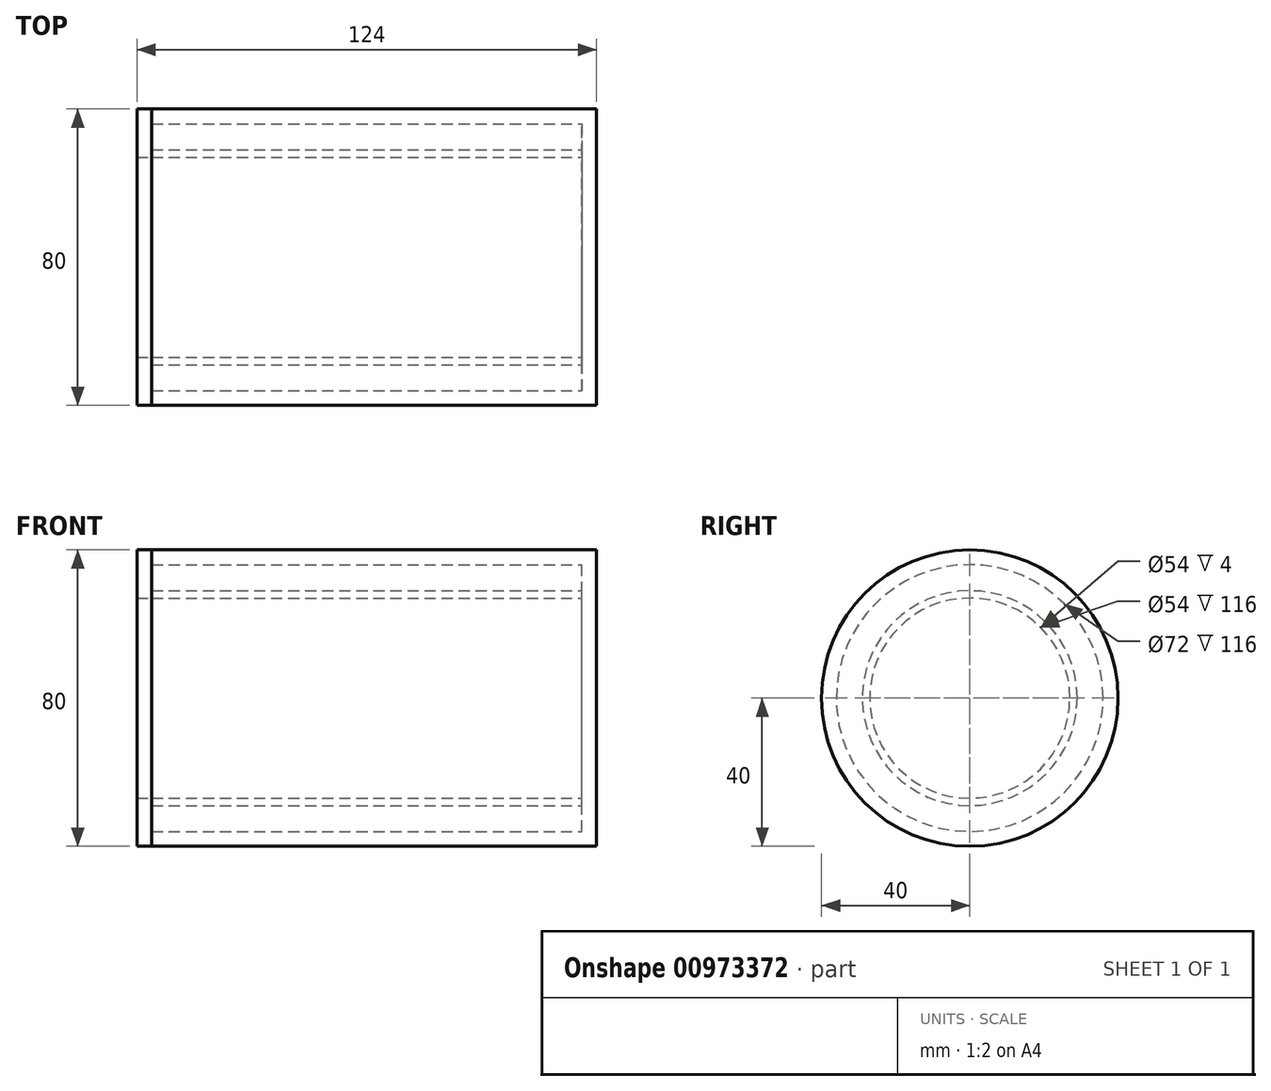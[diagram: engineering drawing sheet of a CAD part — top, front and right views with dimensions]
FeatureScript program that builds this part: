
annotation { "Feature Type Name" : "Feature", "Feature Type Description" : "" }
export const myFeature = defineFeature(function(context is Context, id is Id, definition is map)
    precondition{}
    {
        {
            var Q0;
            Q0=qCreatedBy(makeId("Front.planeOp"),FACE);
            var sketch = newSketch(context, id + "F0", { "sketchPlane" : qUnion([Q0])});
            skLineSegment(sketch, "E0.bottom", {"start": v(60, -2) * mm, "end": v(-60, -2) * mm});
            skLineSegment(sketch, "E0.top", {"start": v(60, 2) * mm, "end": v(-60, 2) * mm});
            skLineSegment(sketch, "E0.left", {"start": v(60, -2) * mm, "end": v(60, 2) * mm});
            skPoint(sketch, "E0.middle", {"position": v(0, 0) * mm});
            skLineSegment(sketch, "E1.bottom", {"start": v(60, -2) * mm, "end": v(56, -2) * mm});
            skLineSegment(sketch, "E1.top", {"start": v(60, -38) * mm, "end": v(56, -38) * mm});
            skLineSegment(sketch, "E1.left", {"start": v(60, -2) * mm, "end": v(60, -38) * mm});
            skLineSegment(sketch, "E1.right", {"start": v(56, -2) * mm, "end": v(56, -38) * mm});
            skLineSegment(sketch, "E2.bottom", {"start": v(-60, -9) * mm, "end": v(56, -9) * mm});
            skLineSegment(sketch, "E2.top", {"start": v(-60, -11) * mm, "end": v(56, -11) * mm});
            skLineSegment(sketch, "E2.right", {"start": v(56, -9) * mm, "end": v(56, -11) * mm});
            skLineSegment(sketch, "E3", {"start": v(-60, 2) * mm, "end": v(-60, -2) * mm});
            skLineSegment(sketch, "E4", {"start": v(-60, -9) * mm, "end": v(-60, -11) * mm});
            skLineSegment(sketch, "E5.bottom", {"start": v(-60, 2) * mm, "end": v(-64, 2) * mm});
            skLineSegment(sketch, "E5.top", {"start": v(-60, -11) * mm, "end": v(-64, -11) * mm});
            skLineSegment(sketch, "E5.left", {"start": v(-60, 2) * mm, "end": v(-60, -11) * mm});
            skLineSegment(sketch, "E5.right", {"start": v(-64, 2) * mm, "end": v(-64, -11) * mm});
            skSolve(sketch);
        }
        {
            var Q0;
            Q0=makeQuery(id+"F0.imprint","IMPRINT",FACE,{"disambiguationData":[TD([[makeQuery(id+"F0.imprint","IMPRINT",EDGE,{"derivedFrom":sQuery(id+"F0.wireOp",EDGE,"E0.top")}),1.0]])]});
            var Q1;
            {var subQ1=sQuery(id+"F0.wireOp",EDGE,"E1.top");Q1=makeQuery(id+"F0.imprint","IMPRINT",FACE,{"disambiguationData":[TD([[makeQuery(id+"F0.imprint","IMPRINT",EDGE,{"derivedFrom":subQ1}),-1.0]])]});}
            var Q2;
            Q2=makeQuery(id+"F0.imprint","IMPRINT",FACE,{"disambiguationData":[TD([[makeQuery(id+"F0.imprint","IMPRINT",EDGE,{"derivedFrom":sQuery(id+"F0.wireOp",EDGE,"E0.right")}),1.0]])]});
            var Q3;
            Q3=sQuery(id+"F0.wireOp",EDGE,"E1.top");
            revolve(context, id + "F1", {"surfaceOperationType" : NewSurfaceOperationType.NEW, "entities" : qUnion([Q0, Q1, Q2]), "axis" : qUnion([Q3]), "revolveType" : RevolveType.FULL});
        }
        {
            var Q0;
            {var subQ1=sQuery(id+"F0.wireOp",EDGE,"E2.bottom");Q0=makeQuery(id+"F0.imprint","IMPRINT",FACE,{"disambiguationData":[TD([[makeQuery(id+"F0.imprint","IMPRINT",EDGE,{"derivedFrom":subQ1}),-1.0]])]});}
            var Q1;
            Q1=makeQuery(id+"F0.imprint","IMPRINT",FACE,{"disambiguationData":[TD([[makeQuery(id+"F0.imprint","IMPRINT",EDGE,{"derivedFrom":sQuery(id+"F0.wireOp",EDGE,"E3")}),-1.0]])]});
            var Q2;
            Q2=sQuery(id+"F0.wireOp",EDGE,"E1.top");
            revolve(context, id + "F2", {"surfaceOperationType" : NewSurfaceOperationType.NEW, "entities" : qUnion([Q0, Q1]), "axis" : qUnion([Q2]), "revolveType" : RevolveType.FULL});
        }
    });
